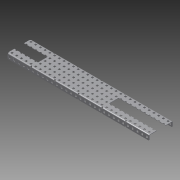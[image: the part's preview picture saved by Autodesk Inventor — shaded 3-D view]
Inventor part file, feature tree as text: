
AUTODESK INVENTOR PART (.ipt)
format: ipt  version: 2012 (Build 160160000, 160)  size: 2,615,296 bytes
history: native  units: in
note: dims shown in document units (in); Inventor stores cm internally (conversion verified against a paired STEP export)
features: extrude x2, sketch x2, other x1, imported_body x1, plane x1, split x1
ambient origin geometry x8: Origin, YZ Plane, XZ Plane, XY Plane, X Axis, Y Axis, Z Axis, Center Point
feature tree (8):
  parser-record x1  (decoder bookkeeping rows leaked as tree rows — omitted from the tree; the rows remain in map.json)
  imported_body  "Base1"
  plane  "Work Plane1"
  split  "Split1"
  extrude  "Extrusion1"  Depth=1.0in TaperAngle=0.0deg
  extrude  "Extrusion2"  [1 undecoded]
  sketch  "Sketch1"  dims[d0=-2.5in d1=1.0in d2=0.0in]
  sketch  "Sketch2"  dims[d3=1.0in d4=0.0in]
note: 1 required parameter value undecoded (feature->parameter linkage not recoverable at this tier; creation-order binding heuristic only, values carry confidence <= 0.55)
